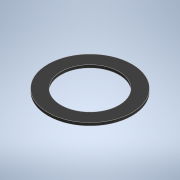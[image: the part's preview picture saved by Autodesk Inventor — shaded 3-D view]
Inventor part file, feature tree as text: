
AUTODESK INVENTOR PART (.ipt)
format: ipt  version: 2022 (Build 260153000, 153)  size: 108,032 bytes
history: native  units: mm
features: extrude x1, sketch x1
ambient origin geometry x8: Origin, YZ Plane, XZ Plane, XY Plane, X Axis, Y Axis, Z Axis, Center Point
bodies: Solid1 (feature_tree)
feature tree (2):
  extrude  "Extrusion1"  Depth=1.0mm
  sketch  "Sketch1"  dims[d0=20.0mm d1=29.0mm d2=1.0mm d3=0.0mm]
